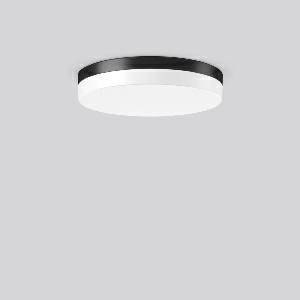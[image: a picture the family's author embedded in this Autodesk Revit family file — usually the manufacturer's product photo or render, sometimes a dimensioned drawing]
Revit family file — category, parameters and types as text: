
# Revit family: flat_slim_round_312632_0031_19_ca4c
name_source: partatom
category: Lighting Fixtures
units: mm (PartAtom-declared; Revit-internal decimal feet)

## family parameters
Cut with Voids When Loaded = No
Host = Face
Light Source = No
Part Type = Normal
Room Calculation Point = No
Round Connector Dimension = Use Diameter
Shared = No

## types (1)
- MultiLumen 1 830 (1 x LED Modul 830, 2400 lm, 3000)
    Apparent Load = 20 VA
    CIE Flux Codes = 39 70 90 83 100
    Color Rendering = 80
    Color Temperature = 3000
    Default Elevation = 1800 mm
    Height = 70 mm
    Lamp = 1 x LED Modul 830
    Lamp Light Flux = 2400 lm
    Lamp count = 1
    Length = 400 mm
    Lifetime = 50000 h
    Luminous efficacy = 120 lm/W
    Manufacturer = RZB
    ModVariant = No
    Model = 312632.0031.19
    Mounting Place = Ceiling
    Mounting Type = Surface mounted
    Number of Poles = 1
    OnlyDefault = Yes
    Power Factor = 1
    Product Name = FLAT SLIM round
    Product group = Surface mounted ceiling and wall luminaires
    ProductGroupID = 305
    Protection Class = Protection class I
    Protection Degree = Degree of protection
    RLX_Detail_Level = 1
    RLX_Emergency_Light_Flux = 0 lm
    RLX_Emergency_Type = 0
    RLX_Emergency_Type_DB = No
    RlxData = <blob elided: 22021 chars, md5=504078d6>
    Socket = socket
    Standby Power = 0 W
    System Light Flux = 2400 lm
    System Power = 20 W
    Type Comments = MultiLumen 1 830
    Type Image = 312631.0031.jpg
    URL = http://relux.com
    VarID = multilumen_1_830
    Voltage = 0 V
    Weight = 0.00 kg
    Width = 0 mm  [stored 0 ft]

note: [stored X ft] marks values corroborated as IEEE doubles in the binary element streams (Revit-internal decimal feet)

## geometry (parser evidence)
native form markers: Blend x4, Sweep x13
no freeform markers — native parametric forms only
